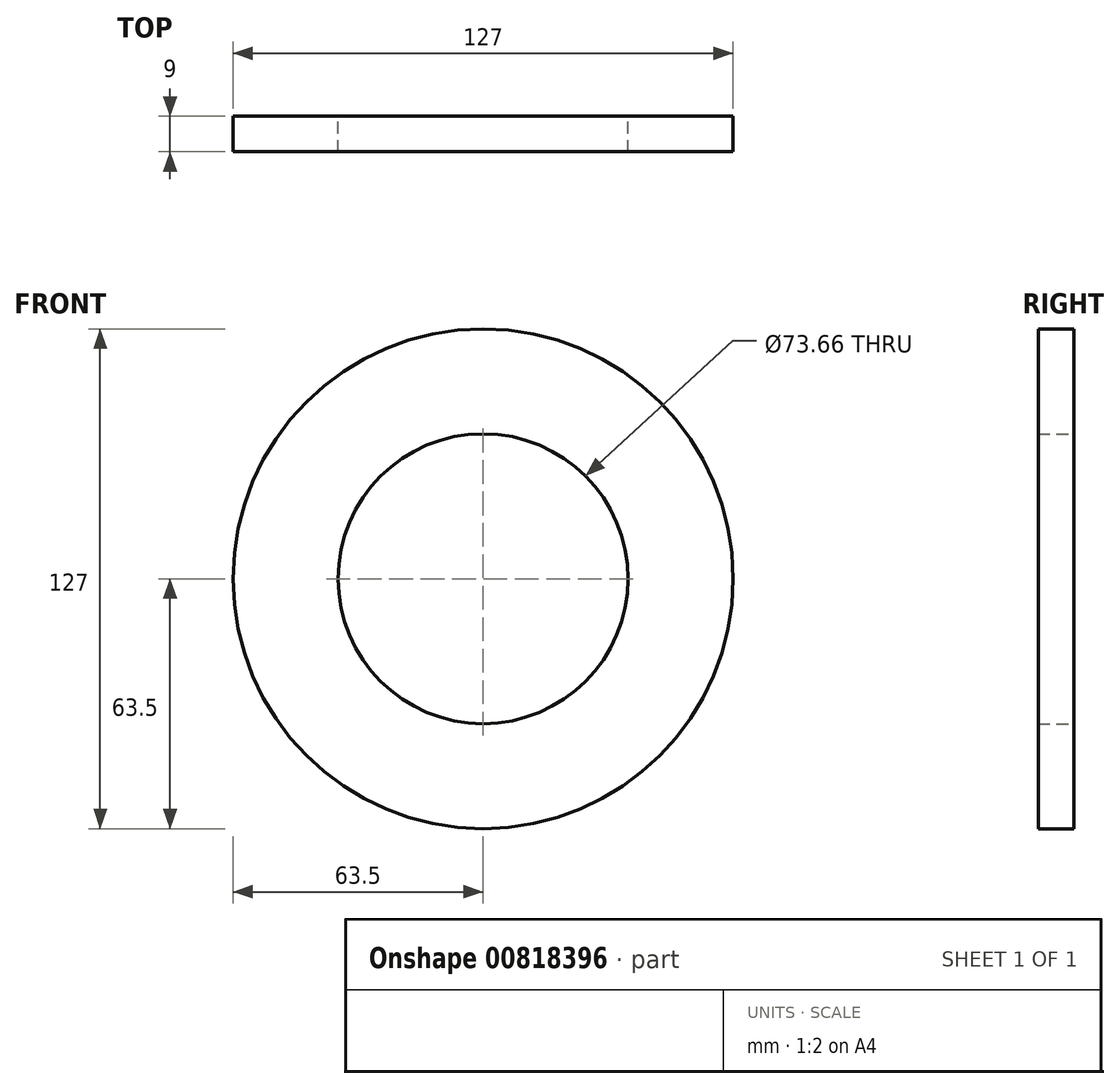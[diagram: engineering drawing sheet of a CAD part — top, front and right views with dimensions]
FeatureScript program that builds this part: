
annotation { "Feature Type Name" : "Feature", "Feature Type Description" : "" }
export const myFeature = defineFeature(function(context is Context, id is Id, definition is map)
    precondition{}
    {
        {
            var Q0;
            Q0=qCreatedBy(makeId("Front.planeOp"),FACE);
            var sketch = newSketch(context, id + "F0", { "sketchPlane" : qUnion([Q0])});
            skCircle(sketch, "E0", {"center": v(0, 0) * mm, "radius": 63.5 * mm});
            skCircle(sketch, "E1", {"center": v(0, 0) * mm, "radius": 36.83 * mm});
            skSolve(sketch);
        }
        {
            var Q0;
            Q0=makeQuery(id+"F0.imprint","IMPRINT",FACE,{"disambiguationData":[TD([[makeQuery(id+"F0.imprint","IMPRINT",EDGE,{"derivedFrom":sQuery(id+"F0.wireOp",EDGE,"E0")}),1.0]])]});
            extrude(context, id + "F1", {"entities" : qUnion([Q0]), "depth" : 9 * mm, "offsetDistance" : 25.4 * mm});
        }
    });
